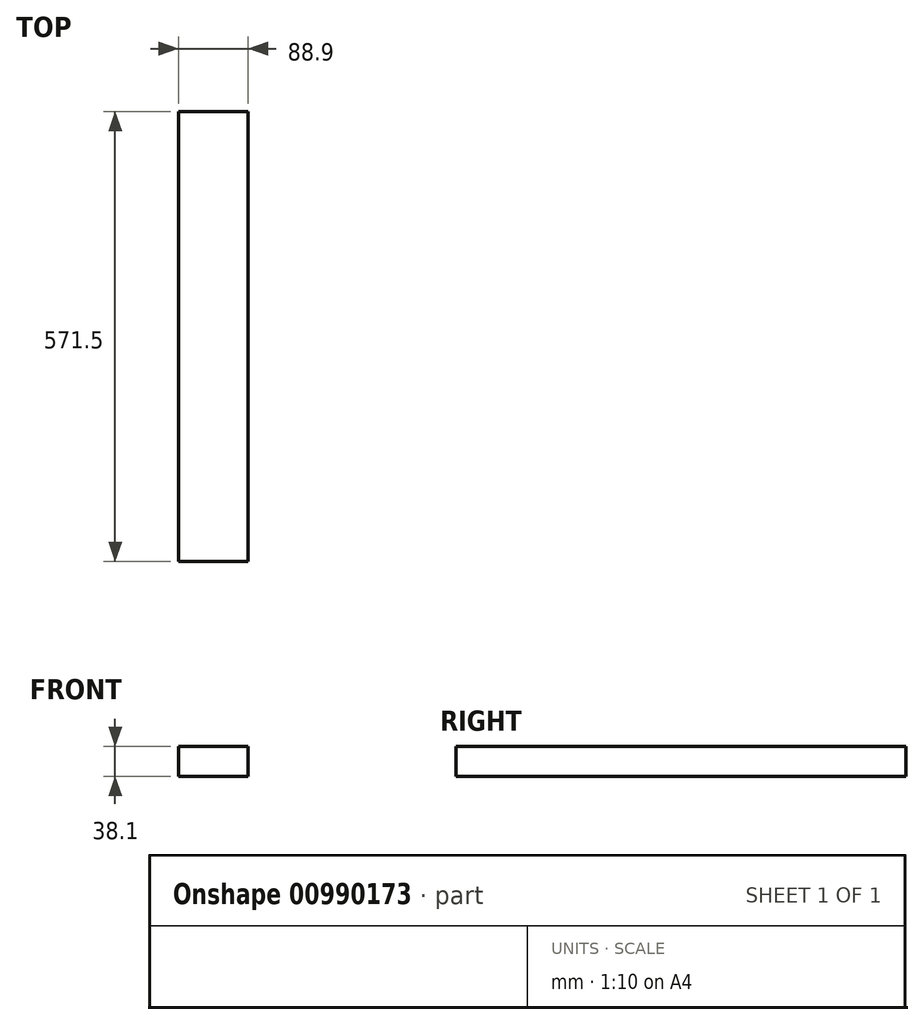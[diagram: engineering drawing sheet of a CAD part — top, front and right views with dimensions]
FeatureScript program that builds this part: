
annotation { "Feature Type Name" : "Feature", "Feature Type Description" : "" }
export const myFeature = defineFeature(function(context is Context, id is Id, definition is map)
    precondition{}
    {
        {
            assignVariable(context, id + "F0", {"name" : "w", "anyValue" : 38.1 * mm});
        }
        {
            var Q0;
            Q0=qCreatedBy(makeId("Top.planeOp"),FACE);
            var sketch = newSketch(context, id + "F1", { "sketchPlane" : qUnion([Q0])});
            skLineSegment(sketch, "E0.bottom", {"start": v(44.45, 285.75) * mm, "end": v(-44.45, 285.75) * mm});
            skLineSegment(sketch, "E0.top", {"start": v(44.45, -285.75) * mm, "end": v(-44.45, -285.75) * mm});
            skLineSegment(sketch, "E0.left", {"start": v(44.45, 285.75) * mm, "end": v(44.45, -285.75) * mm});
            skLineSegment(sketch, "E0.right", {"start": v(-44.45, 285.75) * mm, "end": v(-44.45, -285.75) * mm});
            skPoint(sketch, "E0.middle", {"position": v(0, 0) * mm});
            skSolve(sketch);
        }
        {
            var Q0;
            Q0=qSketchRegion(id+"F1",true);
            extrude(context, id + "F2", {"entities" : qUnion([Q0]), "depth" : getVariable(context, 'w'), "offsetDistance" : 25.4 * mm});
        }
    });
